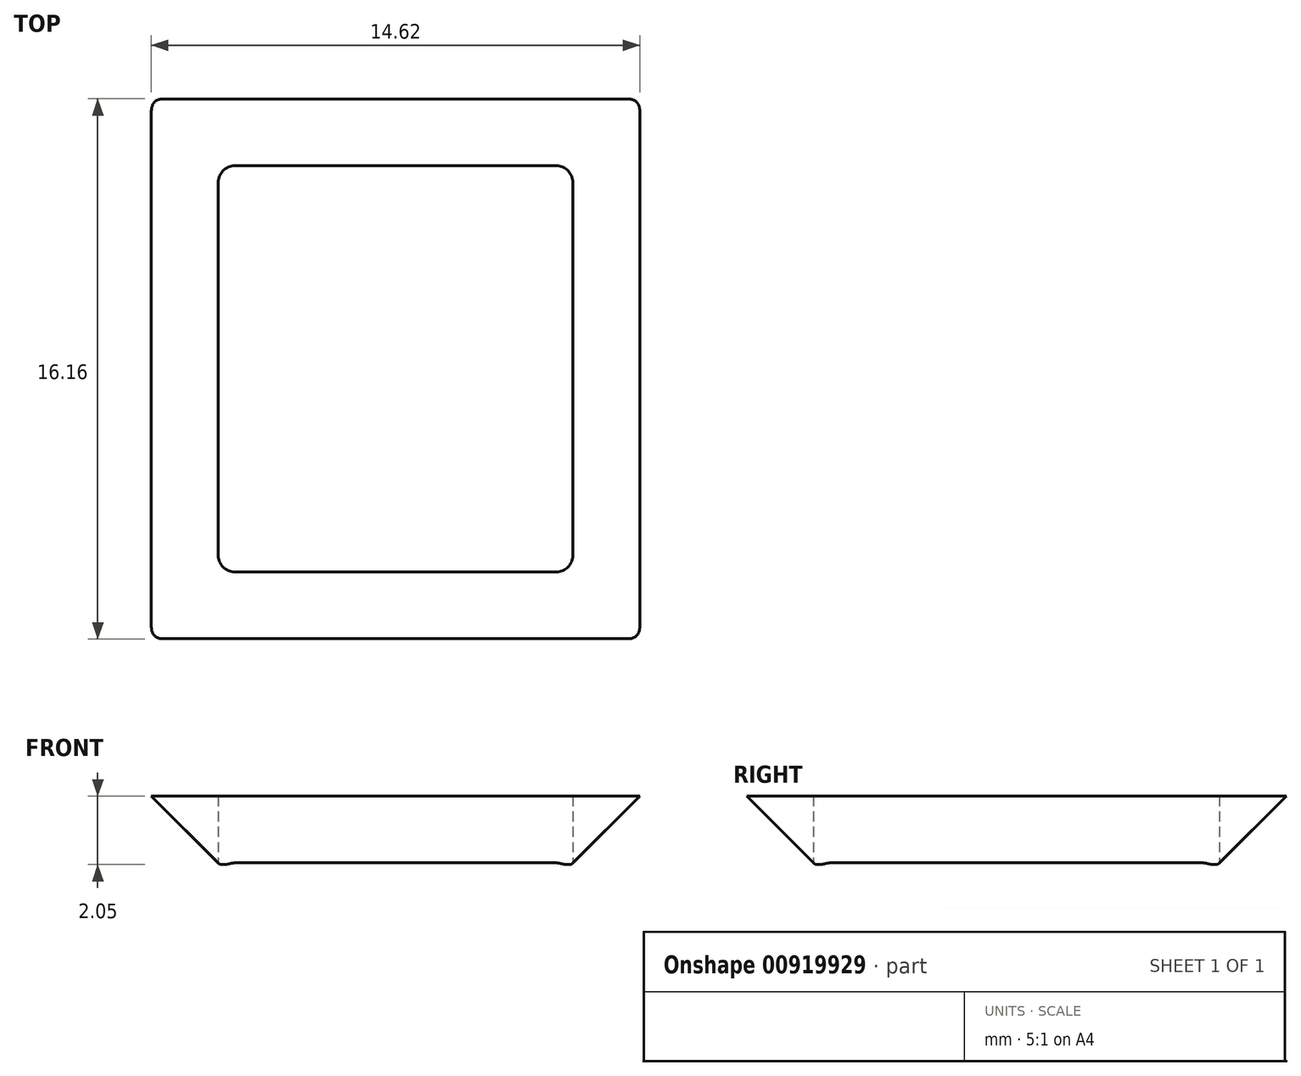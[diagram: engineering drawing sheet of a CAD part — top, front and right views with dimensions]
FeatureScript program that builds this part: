
annotation { "Feature Type Name" : "Feature", "Feature Type Description" : "" }
export const myFeature = defineFeature(function(context is Context, id is Id, definition is map)
    precondition{}
    {
        {
            var Q0;
            Q0=qCreatedBy(makeId("Top.planeOp"),FACE);
            var sketch = newSketch(context, id + "F0", { "sketchPlane" : qUnion([Q0])});
            skLineSegment(sketch, "E0.bottom", {"start": v(5.31, 6.08) * mm, "end": v(-5.3, 6.08) * mm});
            skLineSegment(sketch, "E0.top", {"start": v(5.3, -6.08) * mm, "end": v(-5.31, -6.08) * mm});
            skLineSegment(sketch, "E0.left", {"start": v(5.3, 6.08) * mm, "end": v(5.3, -6.08) * mm});
            skLineSegment(sketch, "E0.right", {"start": v(-5.3, 6.08) * mm, "end": v(-5.31, -6.08) * mm});
            skPoint(sketch, "E0.middle", {"position": v(0, 0) * mm});
            skLineSegment(sketch, "E1.0", {"start": v(7.31, 8.08) * mm, "end": v(-7.3, 8.08) * mm});
            skLineSegment(sketch, "E1.1", {"start": v(7.3, 8.08) * mm, "end": v(7.3, -8.08) * mm});
            skLineSegment(sketch, "E1.2", {"start": v(7.3, -8.08) * mm, "end": v(-7.31, -8.08) * mm});
            skLineSegment(sketch, "E1.3", {"start": v(-7.3, 8.08) * mm, "end": v(-7.31, -8.08) * mm});
            skSolve(sketch);
        }
        {
            var Q0;
            Q0=makeQuery(id+"F0.imprint","IMPRINT",FACE,{"disambiguationData":[TD([[makeQuery(id+"F0.imprint","IMPRINT",EDGE,{"derivedFrom":sQuery(id+"F0.wireOp",EDGE,"E0.bottom")}),-1.0]])]});
            extrude(context, id + "F1", {"entities" : qUnion([Q0]), "depth" : 2 * mm, "offsetDistance" : 25 * mm});
        }
        {
            var Q0;
            Q0=makeQuery(id+"F1.opExtrude","CAP_EDGE",EDGE,{"disambiguationData":[OSD([sQuery(id+"F0.wireOp",EDGE,"E1.1")])],"isStart":true});
            var Q1;
            Q1=makeQuery(id+"F1.opExtrude","CAP_EDGE",EDGE,{"disambiguationData":[OSD([sQuery(id+"F0.wireOp",EDGE,"E1.0")])],"isStart":true});
            var Q2;
            Q2=makeQuery(id+"F1.opExtrude","CAP_EDGE",EDGE,{"disambiguationData":[OSD([sQuery(id+"F0.wireOp",EDGE,"E1.3")])],"isStart":true});
            var Q3;
            Q3=makeQuery(id+"F1.opExtrude","CAP_EDGE",EDGE,{"disambiguationData":[OSD([sQuery(id+"F0.wireOp",EDGE,"E1.2")])],"isStart":true});
            chamfer(context, id + "F2", {"entities" : qUnion([Q0, Q1, Q2, Q3]), "width" : 2 * mm});
        }
        {
            var Q0;
            Q0=makeQuery(id+"F2.opChamfer","BLEND_EDGE",EDGE,{"blendedFrom":[makeQuery(id+"F1.opExtrude","CAP_EDGE",EDGE,{"disambiguationData":[OSD([sQuery(id+"F0.wireOp",EDGE,"E1.0")])],"isStart":true}),makeQuery(id+"F1.opExtrude","CAP_EDGE",EDGE,{"disambiguationData":[OSD([sQuery(id+"F0.wireOp",EDGE,"E1.3")])],"isStart":true})],"blendedInto":[]});
            var Q1;
            Q1=makeQuery(id+"F2.opChamfer","BLEND_EDGE",EDGE,{"blendedFrom":[makeQuery(id+"F1.opExtrude","CAP_EDGE",EDGE,{"disambiguationData":[OSD([sQuery(id+"F0.wireOp",EDGE,"E1.2")])],"isStart":true}),makeQuery(id+"F1.opExtrude","CAP_EDGE",EDGE,{"disambiguationData":[OSD([sQuery(id+"F0.wireOp",EDGE,"E1.3")])],"isStart":true})],"blendedInto":[]});
            var Q2;
            Q2=makeQuery(id+"F2.opChamfer","BLEND_EDGE",EDGE,{"blendedFrom":[makeQuery(id+"F1.opExtrude","CAP_EDGE",EDGE,{"disambiguationData":[OSD([sQuery(id+"F0.wireOp",EDGE,"E1.1")])],"isStart":true}),makeQuery(id+"F1.opExtrude","CAP_EDGE",EDGE,{"disambiguationData":[OSD([sQuery(id+"F0.wireOp",EDGE,"E1.2")])],"isStart":true})],"blendedInto":[]});
            var Q3;
            Q3=makeQuery(id+"F2.opChamfer","BLEND_EDGE",EDGE,{"blendedFrom":[makeQuery(id+"F1.opExtrude","CAP_EDGE",EDGE,{"disambiguationData":[OSD([sQuery(id+"F0.wireOp",EDGE,"E1.0")])],"isStart":true}),makeQuery(id+"F1.opExtrude","CAP_EDGE",EDGE,{"disambiguationData":[OSD([sQuery(id+"F0.wireOp",EDGE,"E1.1")])],"isStart":true})],"blendedInto":[]});
            var Q4;
            Q4=makeQuery(id+"F1.opExtrude","SWEPT_EDGE",EDGE,{"disambiguationData":[OSD([sQuery(id+"F0.wireOp",EDGE,"E0.bottom"),sQuery(id+"F0.wireOp",EDGE,"E0.left")])]});
            var Q5;
            Q5=makeQuery(id+"F1.opExtrude","SWEPT_EDGE",EDGE,{"disambiguationData":[OSD([sQuery(id+"F0.wireOp",EDGE,"E0.bottom"),sQuery(id+"F0.wireOp",EDGE,"E0.right")])]});
            var Q6;
            Q6=makeQuery(id+"F1.opExtrude","SWEPT_EDGE",EDGE,{"disambiguationData":[OSD([sQuery(id+"F0.wireOp",EDGE,"E0.top"),sQuery(id+"F0.wireOp",EDGE,"E0.right")])]});
            var Q7;
            Q7=makeQuery(id+"F1.opExtrude","SWEPT_EDGE",EDGE,{"disambiguationData":[OSD([sQuery(id+"F0.wireOp",EDGE,"E0.top"),sQuery(id+"F0.wireOp",EDGE,"E0.left")])]});
            fillet(context, id + "F3", {"entities" : qUnion([Q0, Q1, Q2, Q3, Q4, Q5, Q6, Q7]), "radius" : .5 * mm, "tangentPropagation" : true, "allowEdgeOverflow" : false});
        }
    });
